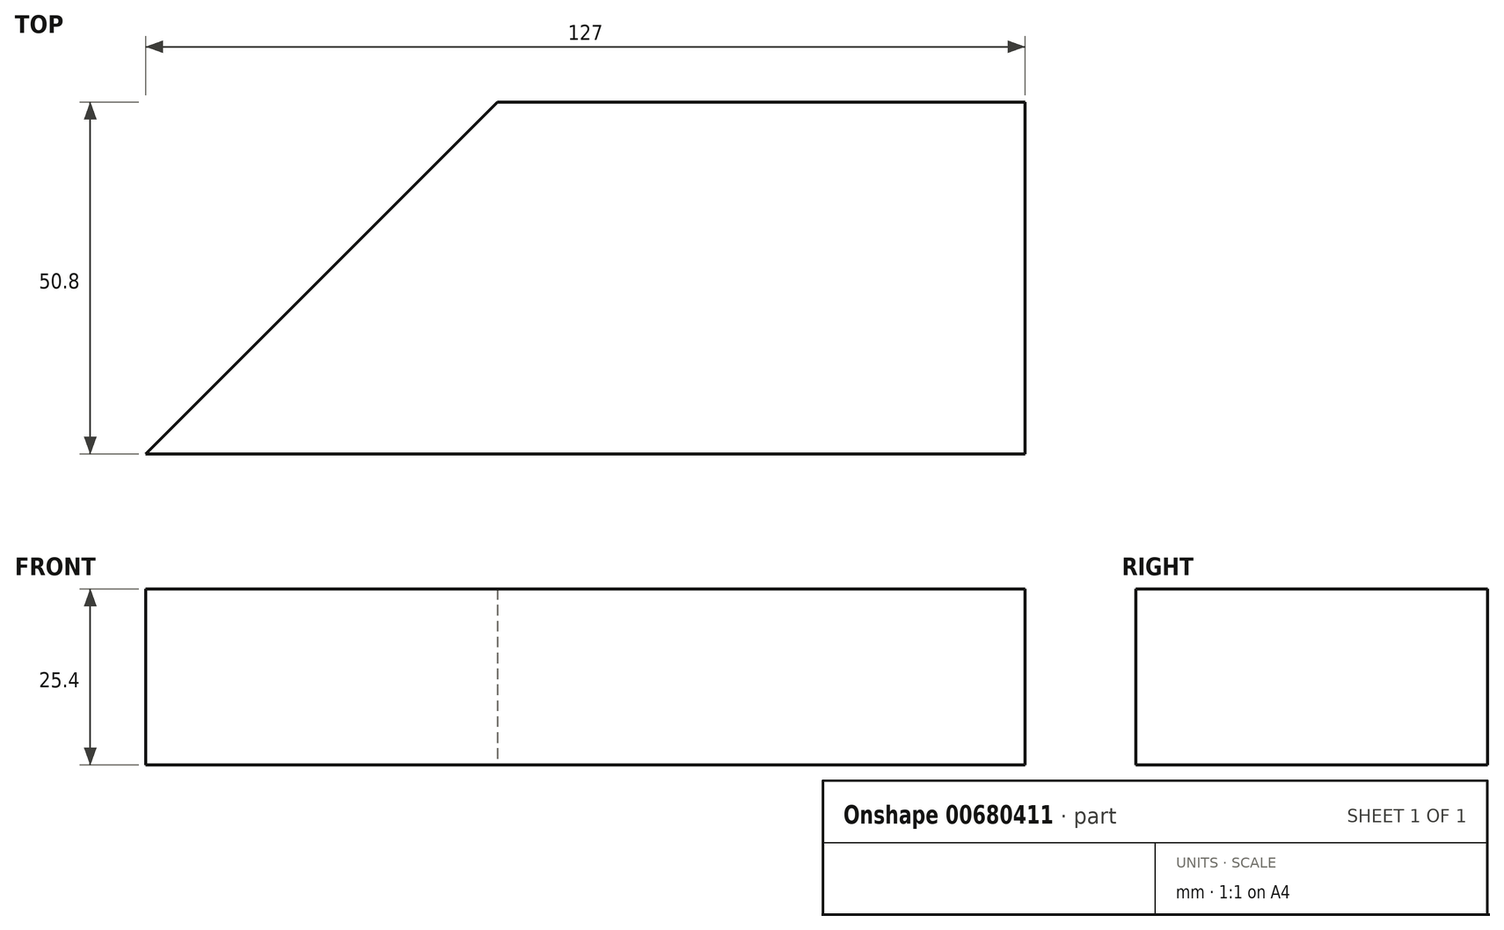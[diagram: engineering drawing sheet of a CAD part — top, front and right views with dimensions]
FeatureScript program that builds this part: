
annotation { "Feature Type Name" : "Feature", "Feature Type Description" : "" }
export const myFeature = defineFeature(function(context is Context, id is Id, definition is map)
    precondition{}
    {
        {
            var Q0;
            Q0=qCreatedBy(makeId("Top.planeOp"),FACE);
            var sketch = newSketch(context, id + "F0", { "sketchPlane" : qUnion([Q0])});
            skLineSegment(sketch, "E0", {"start": v(0, 0) * mm, "end": v(50.8, 50.8) * mm});
            skLineSegment(sketch, "E1", {"start": v(50.8, 50.8) * mm, "end": v(127, 50.8) * mm});
            skLineSegment(sketch, "E2", {"start": v(127, 50.8) * mm, "end": v(127, 0) * mm});
            skLineSegment(sketch, "E3", {"start": v(127, 0) * mm, "end": v(0, 0) * mm});
            skSolve(sketch);
        }
        {
            var Q0;
            Q0=makeQuery(id+"F0.imprint","IMPRINT",FACE,{"disambiguationData":[TD([[makeQuery(id+"F0.imprint","IMPRINT",EDGE,{"derivedFrom":sQuery(id+"F0.wireOp",EDGE,"E0")}),-1.0]])]});
            extrude(context, id + "F1", {"entities" : qUnion([Q0]), "depth" : 25.4 * mm, "offsetDistance" : 25.4 * mm});
        }
    });
